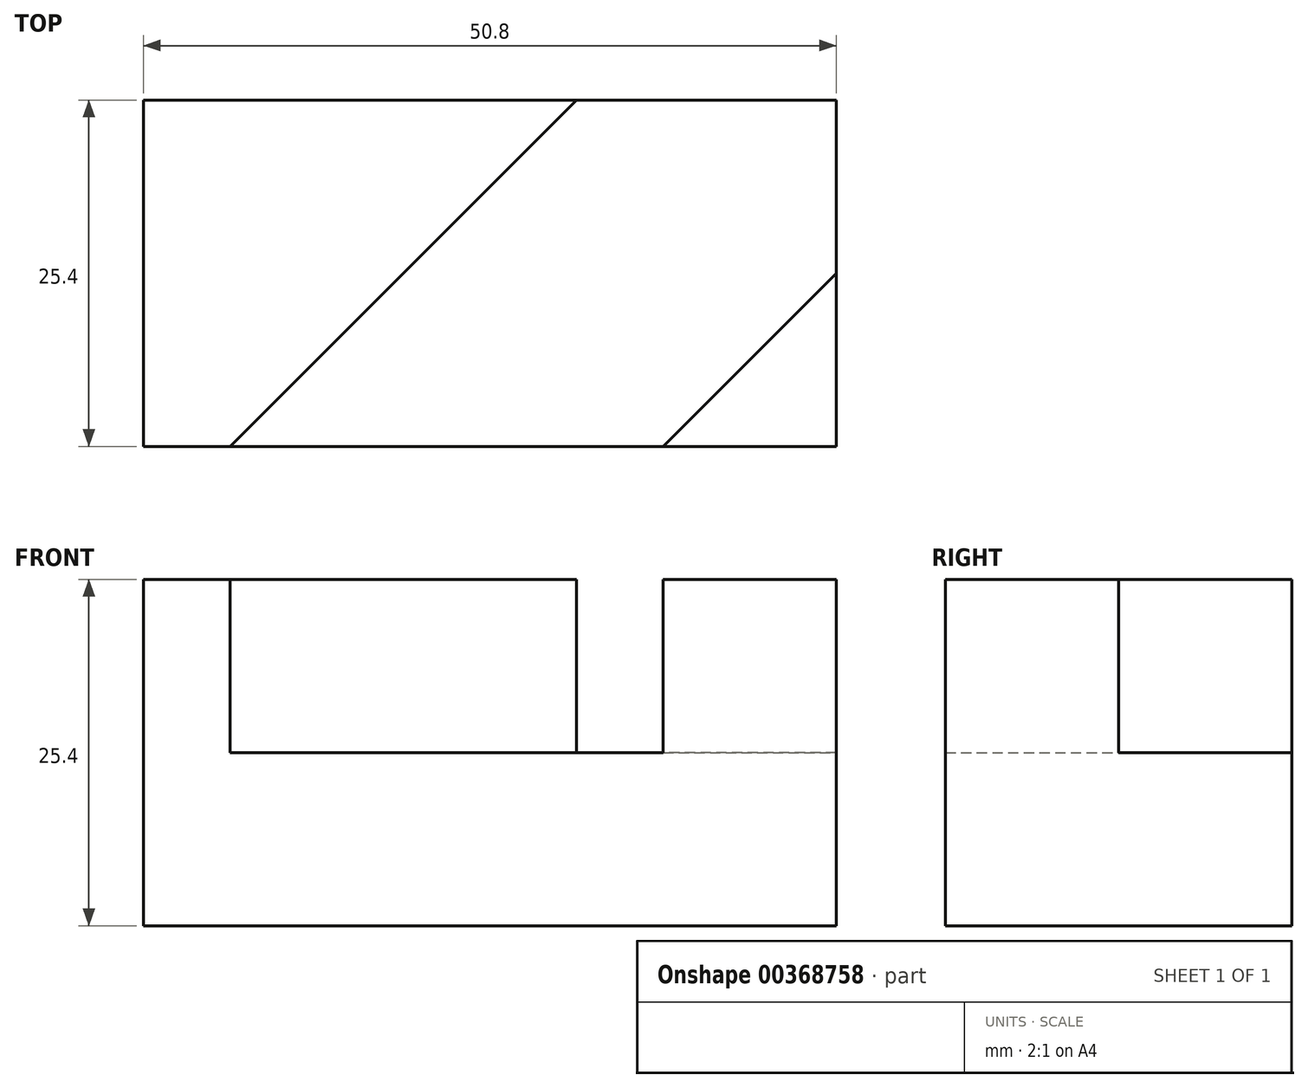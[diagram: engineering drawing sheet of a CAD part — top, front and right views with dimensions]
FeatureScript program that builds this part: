
annotation { "Feature Type Name" : "Feature", "Feature Type Description" : "" }
export const myFeature = defineFeature(function(context is Context, id is Id, definition is map)
    precondition{}
    {
        {
            var Q0;
            Q0=qCreatedBy(makeId("Front.planeOp"),FACE);
            var sketch = newSketch(context, id + "F0", { "sketchPlane" : qUnion([Q0])});
            skLineSegment(sketch, "E0", {"start": v(0, 0) * mm, "end": v(0, 25.4) * mm});
            skLineSegment(sketch, "E1", {"start": v(50.8, 25.4) * mm, "end": v(0, 25.4) * mm});
            skLineSegment(sketch, "E2", {"start": v(50.8, 25.4) * mm, "end": v(50.8, 0) * mm});
            skLineSegment(sketch, "E3", {"start": v(0, 0) * mm, "end": v(50.8, 0) * mm});
            skSolve(sketch);
        }
        {
            var Q0;
            Q0 = qSketchRegion(id + "F0", true);
            extrude(context, id + "F1", {"entities" : qUnion([Q0]), "depth" : 25.4 * mm});
        }
        {
            var Q0;
            Q0=makeQuery(id+"F1.opExtrude","SWEPT_FACE",FACE,{"disambiguationData":[OSD([sQuery(id+"F0.wireOp",EDGE,"E1")])]});
            var sketch = newSketch(context, id + "F2", { "sketchPlane" : qUnion([Q0])});
            skLineSegment(sketch, "E4", {"start": v(6.35, -25.4) * mm, "end": v(31.75, 0) * mm});
            skLineSegment(sketch, "E5", {"start": v(38.1, -25.4) * mm, "end": v(50.8, -12.7) * mm});
            skSolve(sketch);
        }
        {
            var Q0;
            {var subQ5=sQuery(id+"F2.wireOp",EDGE,"E4");Q0=makeQuery(id+"F2.imprint","IMPRINT",FACE,{"disambiguationData":[TD([[makeQuery(id+"F2.imprint","IMPRINT",EDGE,{"derivedFrom":subQ5}),-1.0]])]});}
            var sketch = newSketch(context, id + "F3", { "sketchPlane" : qUnion([Q0])});
            skSolve(sketch);
        }
        {
            var Q0;
            Q0 = qSketchRegion(id + "F3", true);
            var Q1;
            {var subQ5=sQuery(id+"F2.wireOp",EDGE,"E4");Q1=makeQuery(id+"F2.imprint","IMPRINT",FACE,{"disambiguationData":[TD([[makeQuery(id+"F2.imprint","IMPRINT",EDGE,{"derivedFrom":subQ5}),-1.0]])]});}
            extrude(context, id + "F4", {"entities" : qUnion([Q0, Q1]), "operationType" : NewBodyOperationType.REMOVE, "oppositeDirection" : true, "depth" : 12.7 * mm});
        }
    });
